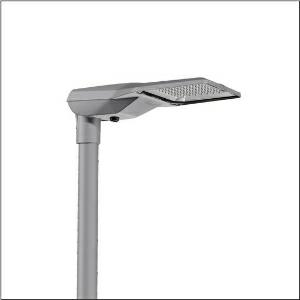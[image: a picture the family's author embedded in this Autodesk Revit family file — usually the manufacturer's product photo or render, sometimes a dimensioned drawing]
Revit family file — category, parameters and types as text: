
# Revit family: streetlight_sl_21_midi___st1_0ab_5xe3m33r08lb_2f09
name_source: partatom
category: Lighting Fixtures
units: mm (PartAtom-declared; Revit-internal decimal feet)

## family parameters
Cut with Voids When Loaded = No
Host = Face
Light Source = No
Part Type = Normal
Room Calculation Point = No
Round Connector Dimension = Use Diameter
Shared = No

## types (1)
- --- (1 x LED, 12620 lm, 99.6 W, 3000K)
    Apparent Load = 100 VA
    CIE Flux Codes = 38 73 97 100 100
    Color Rendering = 70
    Color Temperature = 3000K
    Default Elevation = 1800 mm
    Description = Streetlight SL 21 midi, mast luminaire, primary light control with lens, of PMMA, primary optical cover: cover, of toughened safety glass, transparent, light distribution: ST1.0aB, light emission: direct distribution, primary light characteristic: asymmetric, installation type: side-entry, post-top, LED, High Power LED, rated luminous flux: 12.620lm, luminous efficacy: 127lm/W, light colour: 730, colour temperature: 3000K, control gear: D4i, control: flexible luminous flux parameterisation, time-dependent luminous flux control, constant luminous flux control, overheat protection, pre-setting: logarithmic dimming characteristic, mains connection: 230..240V, AC, 50/60Hz, start of lifetime: 100W, end of service life: 102W, reduction: 46W, luminaire housing, of diecast aluminium, powder-coated, Siteco® metallic grey (DB 702S), corrosivity category C5 mid according to DIN EN ISO 12944, please order mast flange separately, inclination adjustable: 0°, 5°, 10°, 15°, sealing non-destructively replaceable, multi-level sealing system, length: 644mm, width: 335mm, height: 110mm, mast flange for spigot size: 42mm (side-entry): 5XC10008XM4, 60/48mm (side-entry/post-top): 5XC10108XM2, 76/60mm (side-entry/post-top): 5XC10108XM1, mounting height: 4..8m, Smart Interface below, protection rating (complete): IP66, insulation class (complete): insulation class II (safety insulation), certification: CE, ENEC, ENEC+, VDE, impact resistance: IK10, permissible operating ambient temperature for outdoor applications: -40..+50°C, standard-compliant lighting for roads and squares, packaging unit: 1 piece

Light Distribution: ST1.0aB
    Height = 111 mm
    Lamp = 1 x LED
    Lamp Light Flux = 12620 lm
    Lamp Power = 99.6 W
    Lamp count = 1
    Length = 644 mm
    Luminous efficacy = 127 lm/W
    Manufacturer = Siteco
    ModVariant = No
    Model = 5XE3M33R08LB
    Number of Poles = 1
    OnlyDefault = Yes
    Power Factor = 1
    Product Name = Streetlight SL 21 midi | ST1.0aB
    Product group = mast luminaire | pylon top
    ProductGroupID = 6100
    Protection Class = Protection class II
    Protection Degree = IP 66
    RLX_Detail_Level = 1
    RLX_Emergency_Light_Flux = 0 lm
    RLX_Emergency_Type = 0
    RLX_Emergency_Type_DB = No
    RlxData = <blob elided: 26925 chars, md5=1f891564>
    Socket = socket
    Standby Power = 0 W
    System Light Flux = 12620 lm
    System Power = 100 W
    Type Comments = factory setting: luminous flux: 100 % | dim-lin: 254 | 1020 mA
    Type Image = l_1004300.jpg
    URL = http://relux.com
    VarID = @adj_011073
    Voltage = 0 V
    Weight = 0.00 kg
    Width = 336 mm

## geometry (parser evidence)
native form markers: Blend x4, Sweep x10
no freeform markers — native parametric forms only
